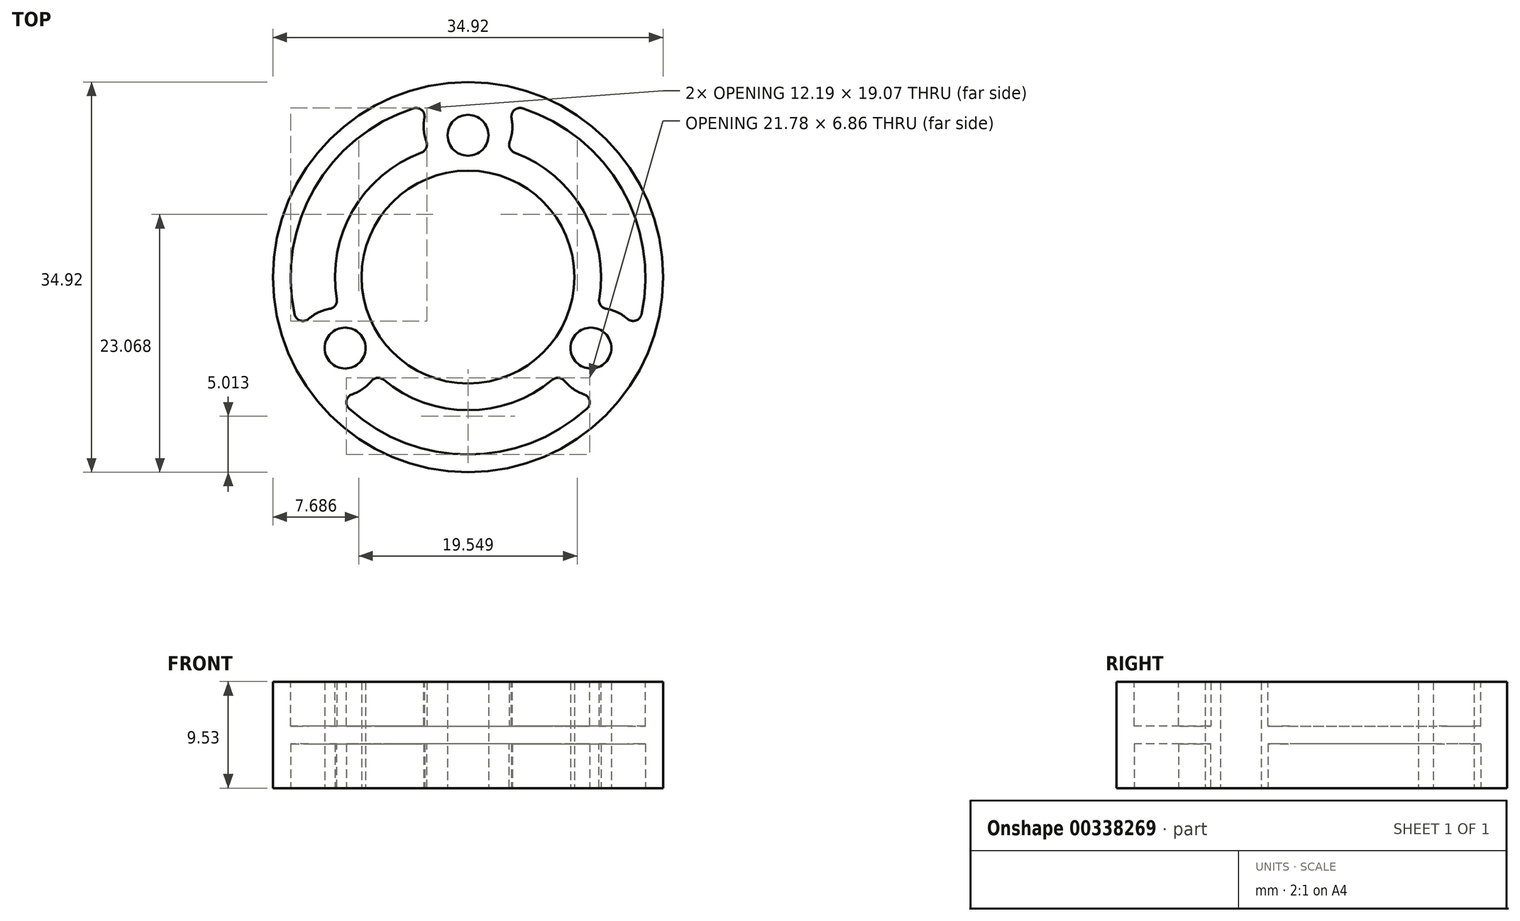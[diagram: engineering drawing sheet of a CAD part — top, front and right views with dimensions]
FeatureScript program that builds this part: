
annotation { "Feature Type Name" : "Feature", "Feature Type Description" : "" }
export const myFeature = defineFeature(function(context is Context, id is Id, definition is map)
    precondition{}
    {
        {
            var Q0;
            Q0=qCreatedBy(makeId("Top.planeOp"),FACE);
            var sketch = newSketch(context, id + "F0", { "sketchPlane" : qUnion([Q0])});
            skCircle(sketch, "E0", {"center": v(0, 0) * mm, "radius": 9.53 * mm});
            skCircle(sketch, "E1", {"center": v(0, 0) * mm, "radius": 17.46 * mm});
            skLineSegment(sketch, "E2", {"start": v(0, 0) * mm, "end": v(0, 12.7) * mm, "construction": true});
            skCircle(sketch, "E3", {"center": v(0, 12.7) * mm, "radius": 1.83 * mm});
            skLineSegment(sketch, "E4", {"start": v(0, 0) * mm, "end": v(11, -6.35) * mm, "construction": true});
            skLineSegment(sketch, "E5", {"start": v(11, -6.35) * mm, "end": v(-11, -6.35) * mm, "construction": true});
            skLineSegment(sketch, "E6", {"start": v(-11, -6.35) * mm, "end": v(0, 0) * mm, "construction": true});
            skLineSegment(sketch, "E7", {"start": v(0, 12.7) * mm, "end": v(11, -6.35) * mm, "construction": true});
            skLineSegment(sketch, "E8", {"start": v(-11, -6.35) * mm, "end": v(0, 12.7) * mm, "construction": true});
            skCircle(sketch, "E9", {"center": v(-11, -6.35) * mm, "radius": 1.83 * mm});
            skCircle(sketch, "E10", {"center": v(11, -6.35) * mm, "radius": 1.83 * mm});
            skSolve(sketch);
        }
        {
            var Q0;
            Q0=qSketchRegion(id+"F0",true);
            extrude(context, id + "F1", {"entities" : qUnion([Q0]), "depth" : 9.52 * mm});
        }
        {
            var Q0;
            {var subQ0=sQuery(id+"F0.wireOp",EDGE,"E1");var subQ1=makeQuery(id+"F1.opExtrude","CAP_FACE",FACE,{"disambiguationData":[OSD([sQuery(id+"F0.wireOp",EDGE,"E0"),subQ0,sQuery(id+"F0.wireOp",EDGE,"E3")])],"isStart":false});Q0=makeQuery(id+"FaGNQa3NOKQJJ3d_1.boolean.opBoolean","SPLIT",FACE,{"disambiguationData":[TD([subQ1,makeQuery(id+"F1.opExtrude","SWEPT_FACE",FACE,{"disambiguationData":[OSD([subQ0])]}),makeQuery(id+"FBX2u8IMGBDlIgd_1.boolean.opBoolean","COPY",FACE,{"derivedFrom":makeQuery(id+"FBX2u8IMGBDlIgd_1.opExtrude","SWEPT_FACE",FACE,{"disambiguationData":[OSD([sQuery(id+"F7rsySl2JD6qCkH_1.wireOp",EDGE,"BS3xaHe7-TctR-HWj4-VqEs-X0m0ugFKdukP")])]})}),makeQuery(id+"FaGNQa3NOKQJJ3d_1.opExtrude","SWEPT_FACE",FACE,{"disambiguationData":[OSD([sQuery(id+"FimIUrEkqtjUp3z_1.wireOp",EDGE,"HlGXKecl-ggte-uXjZ-GF2z-oe2yHpBcJ9Dq")])]}),makeQuery(id+"FaGNQa3NOKQJJ3d_1.opExtrude","SWEPT_FACE",FACE,{"disambiguationData":[OSD([sQuery(id+"FimIUrEkqtjUp3z_1.wireOp",EDGE,"b06J7RxP-un1X-OzPm-o8VI-wkIMPVGFyDBE")])]})])],"derivedFrom":subQ1});}
            var sketch = newSketch(context, id + "F2", { "sketchPlane" : qUnion([Q0])});
            skArc(sketch, "E11", {"start": v(-3.42, 15.5) * mm, "mid": v(-3.97, 13.45) * mm, "end": v(-3.38, 11.42) * mm});
            skArc(sketch, "E12", {"start": v(-3.38, 11.42) * mm, "mid": v(-10.31, 5.95) * mm, "end": v(-11.58, -2.78) * mm});
            skArc(sketch, "E13", {"start": v(-3.42, 15.5) * mm, "mid": v(-13.75, 7.94) * mm, "end": v(-15.14, -4.79) * mm});
            skLineSegment(sketch, "E14", {"start": v(0, 0) * mm, "end": v(0, 13.5) * mm, "construction": true});
            skArc(sketch, "E15", {"start": v(-11.58, -2.78) * mm, "mid": v(-13.63, -3.29) * mm, "end": v(-15.14, -4.79) * mm});
            skArc(sketch, "E16", {"start": v(-15.14, -4.79) * mm, "mid": v(-9.74, -10.2) * mm, "end": v(-11.58, -2.78) * mm, "construction": true});
            skLineSegment(sketch, "E17", {"start": v(-11.69, -6.75) * mm, "end": v(0, 0) * mm, "construction": true});
            skSolve(sketch);
        }
        {
            var Q0;
            Q0=qSketchRegion(id+"F2",true);
            extrude(context, id + "F3", {"entities" : qUnion([Q0]), "operationType" : NewBodyOperationType.REMOVE, "oppositeDirection" : true, "depth" : 3.97 * mm});
        }
        {
            var Q0;
            Q0=makeQuery(id+"F1.opExtrude","CAP_FACE",FACE,{"disambiguationData":[OSD([sQuery(id+"F0.wireOp",EDGE,"E0"),sQuery(id+"F0.wireOp",EDGE,"E1"),sQuery(id+"F0.wireOp",EDGE,"E3")])],"isStart":true});
            var sketch = newSketch(context, id + "F4", { "sketchPlane" : qUnion([Q0])});
            skArc(sketch, "E18", {"start": v(-15.14, 4.79) * mm, "mid": v(-13.75, -7.94) * mm, "end": v(-3.42, -15.5) * mm});
            skArc(sketch, "E19", {"start": v(-11.58, 2.78) * mm, "mid": v(-10.31, -5.95) * mm, "end": v(-3.38, -11.42) * mm});
            skArc(sketch, "E20", {"start": v(-15.14, 4.79) * mm, "mid": v(-13.63, 3.29) * mm, "end": v(-11.58, 2.78) * mm});
            skArc(sketch, "E21", {"start": v(-3.38, -11.42) * mm, "mid": v(-3.97, -13.45) * mm, "end": v(-3.42, -15.5) * mm});
            skSolve(sketch);
        }
        {
            var Q0;
            Q0=qSketchRegion(id+"F4",true);
            extrude(context, id + "F5", {"entities" : qUnion([Q0]), "operationType" : NewBodyOperationType.REMOVE, "oppositeDirection" : true, "depth" : 3.97 * mm});
        }
        {
            var Q0;
            Q0=makeQuery(id+"F3.boolean.opBoolean","COPY",EDGE,{"derivedFrom":makeQuery(id+"F3.opExtrude","SWEPT_EDGE",EDGE,{"disambiguationData":[OSD([sQuery(id+"F2.wireOp",EDGE,"E13"),sQuery(id+"F2.wireOp",EDGE,"E15")])]})});
            var Q1;
            Q1=makeQuery(id+"F3.boolean.opBoolean","COPY",EDGE,{"derivedFrom":makeQuery(id+"F3.opExtrude","SWEPT_EDGE",EDGE,{"disambiguationData":[OSD([sQuery(id+"F2.wireOp",EDGE,"E12"),sQuery(id+"F2.wireOp",EDGE,"E15")])]})});
            var Q2;
            Q2=makeQuery(id+"F3.boolean.opBoolean","COPY",EDGE,{"derivedFrom":makeQuery(id+"F3.opExtrude","SWEPT_EDGE",EDGE,{"disambiguationData":[OSD([sQuery(id+"F2.wireOp",EDGE,"E11"),sQuery(id+"F2.wireOp",EDGE,"E12")])]})});
            var Q3;
            Q3=makeQuery(id+"F3.boolean.opBoolean","COPY",EDGE,{"derivedFrom":makeQuery(id+"F3.opExtrude","SWEPT_EDGE",EDGE,{"disambiguationData":[OSD([sQuery(id+"F2.wireOp",EDGE,"E11"),sQuery(id+"F2.wireOp",EDGE,"E13")])]})});
            var Q4;
            Q4=makeQuery(id+"F5.boolean.opBoolean","COPY",EDGE,{"derivedFrom":makeQuery(id+"F5.opExtrude","SWEPT_EDGE",EDGE,{"disambiguationData":[OSD([sQuery(id+"F4.wireOp",EDGE,"E19"),sQuery(id+"F4.wireOp",EDGE,"E21")])]})});
            var Q5;
            Q5=makeQuery(id+"F5.boolean.opBoolean","COPY",EDGE,{"derivedFrom":makeQuery(id+"F5.opExtrude","SWEPT_EDGE",EDGE,{"disambiguationData":[OSD([sQuery(id+"F4.wireOp",EDGE,"E18"),sQuery(id+"F4.wireOp",EDGE,"E21")])]})});
            var Q6;
            Q6=makeQuery(id+"F5.boolean.opBoolean","COPY",EDGE,{"derivedFrom":makeQuery(id+"F5.opExtrude","SWEPT_EDGE",EDGE,{"disambiguationData":[OSD([sQuery(id+"F4.wireOp",EDGE,"E19"),sQuery(id+"F4.wireOp",EDGE,"E20")])]})});
            var Q7;
            Q7=makeQuery(id+"F5.boolean.opBoolean","COPY",EDGE,{"derivedFrom":makeQuery(id+"F5.opExtrude","SWEPT_EDGE",EDGE,{"disambiguationData":[OSD([sQuery(id+"F4.wireOp",EDGE,"E18"),sQuery(id+"F4.wireOp",EDGE,"E20")])]})});
            fillet(context, id + "F6", {"entities" : qUnion([Q0, Q1, Q2, Q3, Q4, Q5, Q6, Q7]), "radius" : 0.76 * mm, "tangentPropagation" : true, "allowEdgeOverflow" : false});
        }
        {
            var Q0;
            Q0=makeQuery(id+"F6.opFillet","BLEND_FACE",FACE,{"disambiguationData":[OSD([sQuery(id+"F2.wireOp",EDGE,"E13"),sQuery(id+"F2.wireOp",EDGE,"E15")])]});
            var Q1;
            Q1=makeQuery(id+"F3.boolean.opBoolean","COPY",FACE,{"derivedFrom":makeQuery(id+"F3.opExtrude","SWEPT_FACE",FACE,{"disambiguationData":[OSD([sQuery(id+"F2.wireOp",EDGE,"E15")])]})});
            var Q2;
            Q2=makeQuery(id+"F6.opFillet","BLEND_FACE",FACE,{"disambiguationData":[OSD([sQuery(id+"F2.wireOp",EDGE,"E12"),sQuery(id+"F2.wireOp",EDGE,"E15")])]});
            var Q3;
            Q3=makeQuery(id+"F3.boolean.opBoolean","COPY",FACE,{"derivedFrom":makeQuery(id+"F3.opExtrude","SWEPT_FACE",FACE,{"disambiguationData":[OSD([sQuery(id+"F2.wireOp",EDGE,"E12")])]})});
            var Q4;
            Q4=makeQuery(id+"F6.opFillet","BLEND_FACE",FACE,{"disambiguationData":[OSD([sQuery(id+"F2.wireOp",EDGE,"E11"),sQuery(id+"F2.wireOp",EDGE,"E12")])]});
            var Q5;
            Q5=makeQuery(id+"F3.boolean.opBoolean","COPY",FACE,{"derivedFrom":makeQuery(id+"F3.opExtrude","SWEPT_FACE",FACE,{"disambiguationData":[OSD([sQuery(id+"F2.wireOp",EDGE,"E11")])]})});
            var Q6;
            Q6=makeQuery(id+"F6.opFillet","BLEND_FACE",FACE,{"disambiguationData":[OSD([sQuery(id+"F2.wireOp",EDGE,"E11"),sQuery(id+"F2.wireOp",EDGE,"E13")])]});
            var Q7;
            Q7=makeQuery(id+"F3.boolean.opBoolean","COPY",FACE,{"derivedFrom":makeQuery(id+"F3.opExtrude","SWEPT_FACE",FACE,{"disambiguationData":[OSD([sQuery(id+"F2.wireOp",EDGE,"E13")])]})});
            var Q8;
            Q8=makeQuery(id+"F6.opFillet","BLEND_FACE",FACE,{"disambiguationData":[OSD([sQuery(id+"F4.wireOp",EDGE,"E18"),sQuery(id+"F4.wireOp",EDGE,"E20")])]});
            var Q9;
            Q9=makeQuery(id+"F5.boolean.opBoolean","COPY",FACE,{"derivedFrom":makeQuery(id+"F5.opExtrude","SWEPT_FACE",FACE,{"disambiguationData":[OSD([sQuery(id+"F4.wireOp",EDGE,"E20")])]})});
            var Q10;
            Q10=makeQuery(id+"F6.opFillet","BLEND_FACE",FACE,{"disambiguationData":[OSD([sQuery(id+"F4.wireOp",EDGE,"E19"),sQuery(id+"F4.wireOp",EDGE,"E20")])]});
            var Q11;
            Q11=makeQuery(id+"F5.boolean.opBoolean","COPY",FACE,{"derivedFrom":makeQuery(id+"F5.opExtrude","SWEPT_FACE",FACE,{"disambiguationData":[OSD([sQuery(id+"F4.wireOp",EDGE,"E19")])]})});
            var Q12;
            Q12=makeQuery(id+"F6.opFillet","BLEND_FACE",FACE,{"disambiguationData":[OSD([sQuery(id+"F4.wireOp",EDGE,"E19"),sQuery(id+"F4.wireOp",EDGE,"E21")])]});
            var Q13;
            Q13=makeQuery(id+"F5.boolean.opBoolean","COPY",FACE,{"derivedFrom":makeQuery(id+"F5.opExtrude","SWEPT_FACE",FACE,{"disambiguationData":[OSD([sQuery(id+"F4.wireOp",EDGE,"E21")])]})});
            var Q14;
            Q14=makeQuery(id+"F6.opFillet","BLEND_FACE",FACE,{"disambiguationData":[OSD([sQuery(id+"F4.wireOp",EDGE,"E18"),sQuery(id+"F4.wireOp",EDGE,"E21")])]});
            var Q15;
            Q15=makeQuery(id+"F5.boolean.opBoolean","COPY",FACE,{"derivedFrom":makeQuery(id+"F5.opExtrude","SWEPT_FACE",FACE,{"disambiguationData":[OSD([sQuery(id+"F4.wireOp",EDGE,"E18")])]})});
            var Q16;
            Q16=makeQuery(id+"F3.boolean.opBoolean","COPY",FACE,{"derivedFrom":makeQuery(id+"F3.opExtrude","CAP_FACE",FACE,{"disambiguationData":[OSD([sQuery(id+"F2.wireOp",EDGE,"E11"),sQuery(id+"F2.wireOp",EDGE,"E12"),sQuery(id+"F2.wireOp",EDGE,"E13"),sQuery(id+"F2.wireOp",EDGE,"E15")])],"isStart":false})});
            var Q17;
            Q17=makeQuery(id+"F5.boolean.opBoolean","COPY",FACE,{"derivedFrom":makeQuery(id+"F5.opExtrude","CAP_FACE",FACE,{"disambiguationData":[OSD([sQuery(id+"F4.wireOp",EDGE,"E18"),sQuery(id+"F4.wireOp",EDGE,"E19"),sQuery(id+"F4.wireOp",EDGE,"E20"),sQuery(id+"F4.wireOp",EDGE,"E21")])],"isStart":false})});
            var Q18;
            Q18=makeQuery(id+"F1.opExtrude","SWEPT_FACE",FACE,{"disambiguationData":[OSD([sQuery(id+"F0.wireOp",EDGE,"E0")])]});
            circularPattern(context, id + "F7", {"patternType" : PatternType.FACE, "faces" : qUnion([Q0, Q1, Q2, Q3, Q4, Q5, Q6, Q7, Q8, Q9, Q10, Q11, Q12, Q13, Q14, Q15, Q16, Q17]), "axis" : qUnion([Q18]), "angle" : 360 * degree, "instanceCount" : 3, "equalSpace" : true});
        }
    });
